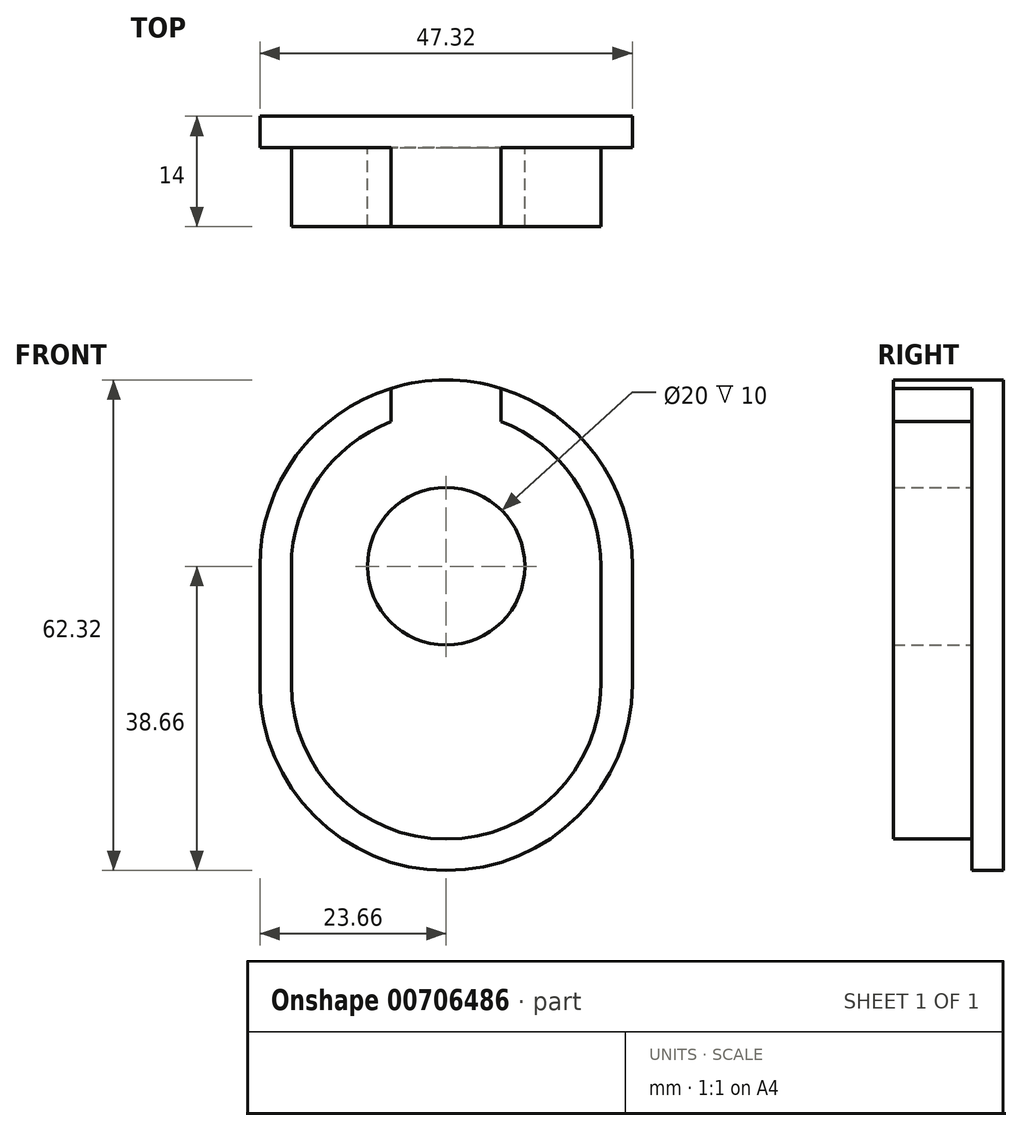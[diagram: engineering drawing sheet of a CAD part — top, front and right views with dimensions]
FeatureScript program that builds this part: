
annotation { "Feature Type Name" : "Feature", "Feature Type Description" : "" }
export const myFeature = defineFeature(function(context is Context, id is Id, definition is map)
    precondition{}
    {
        {
            var Q0;
            Q0=qCreatedBy(makeId("Front.planeOp"),FACE);
            var sketch = newSketch(context, id + "F0", { "sketchPlane" : qUnion([Q0])});
            skCircle(sketch, "E0", {"center": v(0, 0) * mm, "radius": 10 * mm});
            skArc(sketch, "E1", {"start": v(-19.66, 0) * mm, "mid": v(-16.19, 11.16) * mm, "end": v(-7, 18.37) * mm});
            skArc(sketch, "E2", {"start": v(19.66, 0) * mm, "mid": v(16.18, 11.17) * mm, "end": v(6.98, 18.38) * mm});
            skLineSegment(sketch, "E3", {"start": v(-19.66, 0) * mm, "end": v(-19.66, -15) * mm});
            skLineSegment(sketch, "E4", {"start": v(19.66, 0) * mm, "end": v(19.66, -15) * mm});
            skArc(sketch, "E5", {"start": v(-19.66, -15) * mm, "mid": v(0, -34.66) * mm, "end": v(19.66, -15) * mm});
            skArc(sketch, "E6", {"start": v(-23.66, 0) * mm, "mid": v(-11.61, 20.62) * mm, "end": v(12.27, 20.23) * mm});
            skArc(sketch, "E7", {"start": v(23.66, 0) * mm, "mid": v(20.62, 11.61) * mm, "end": v(12.27, 20.23) * mm});
            skLineSegment(sketch, "E8", {"start": v(-23.66, 0) * mm, "end": v(-23.66, -15) * mm});
            skLineSegment(sketch, "E9", {"start": v(23.66, 0) * mm, "end": v(23.66, -15) * mm});
            skArc(sketch, "E10", {"start": v(-23.66, -15) * mm, "mid": v(0, -38.66) * mm, "end": v(23.66, -15) * mm});
            skLineSegment(sketch, "E11", {"start": v(-7, 18.37) * mm, "end": v(-7, 22.6) * mm});
            skPoint(sketch, "E12.start.orphan", {"position": v(7, 18.37) * mm});
            skLineSegment(sketch, "E13", {"start": v(6.98, 18.38) * mm, "end": v(6.98, 22.6) * mm});
            skSolve(sketch);
        }
        {
            var Q0;
            Q0=makeQuery(id+"F0.imprint","IMPRINT",FACE,{"disambiguationData":[TD([[makeQuery(id+"F0.imprint","IMPRINT",EDGE,{"derivedFrom":sQuery(id+"F0.wireOp",EDGE,"E1")}),1.0]])]});
            extrude(context, id + "F1", {"entities" : qUnion([Q0]), "depth" : 10 * mm, "offsetDistance" : 25 * mm});
        }
        {
            var Q0;
            Q0 = qSketchRegion(id + "F0", true);
            var Q1;
            Q1=makeQuery(id+"F0.imprint","IMPRINT",FACE,{"disambiguationData":[TD([[makeQuery(id+"F0.imprint","IMPRINT",EDGE,{"derivedFrom":sQuery(id+"F0.wireOp",EDGE,"E0")}),1.0]])]});
            extrude(context, id + "F2", {"entities" : qUnion([Q0, Q1]), "operationType" : NewBodyOperationType.ADD, "depth" : -4 * mm, "offsetDistance" : 25 * mm});
        }
    });
